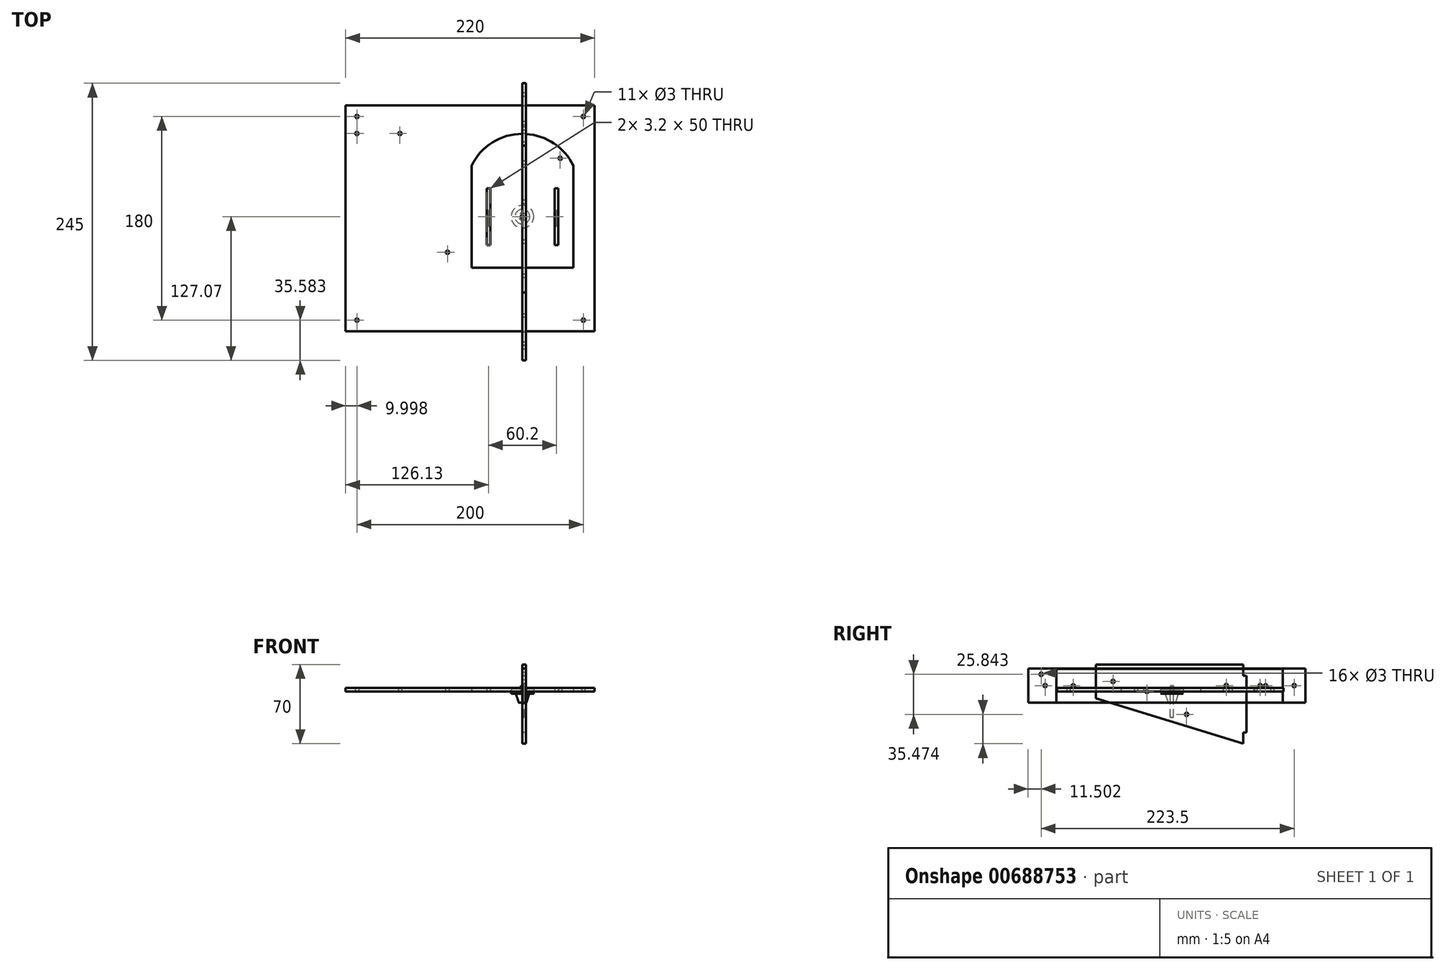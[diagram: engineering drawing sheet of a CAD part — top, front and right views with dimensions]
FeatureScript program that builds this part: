
annotation { "Feature Type Name" : "Feature", "Feature Type Description" : "" }
export const myFeature = defineFeature(function(context is Context, id is Id, definition is map)
    precondition{}
    {
        {
            var Q0;
            Q0=qCreatedBy(makeId("Right.planeOp"),FACE);
            var sketch = newSketch(context, id + "F0", { "sketchPlane" : qUnion([Q0])});
            skLineSegment(sketch, "E0", {"start": v(-67.11, 23.84) * mm, "end": v(62.89, 23.84) * mm});
            skLineSegment(sketch, "E1", {"start": v(-67.11, 23.84) * mm, "end": v(-67.11, -6.16) * mm});
            skLineSegment(sketch, "E2", {"start": v(62.89, 23.84) * mm, "end": v(62.89, -46.16) * mm});
            skLineSegment(sketch, "E3", {"start": v(-67.11, -6.16) * mm, "end": v(62.89, -46.16) * mm});
            skLineSegment(sketch, "E4.bottom", {"start": v(62.89, 13.84) * mm, "end": v(65.89, 13.84) * mm});
            skLineSegment(sketch, "E4.top", {"start": v(62.89, -36.16) * mm, "end": v(65.89, -36.16) * mm});
            skLineSegment(sketch, "E4.left", {"start": v(62.89, 13.84) * mm, "end": v(62.89, -36.16) * mm});
            skLineSegment(sketch, "E4.right", {"start": v(65.89, 13.84) * mm, "end": v(65.89, -36.16) * mm});
            skCircle(sketch, "E5", {"center": v(12.89, -20.32) * mm, "radius": 1.5 * mm});
            skSolve(sketch);
        }
        {
            var Q0;
            Q0=qCreatedBy(makeId("Right.planeOp"),FACE);
            var sketch = newSketch(context, id + "F1", { "sketchPlane" : qUnion([Q0])});
            skLineSegment(sketch, "E6.bottom", {"start": v(-127.07, 20.16) * mm, "end": v(117.93, 20.16) * mm});
            skLineSegment(sketch, "E6.top", {"start": v(-127.07, -9.84) * mm, "end": v(117.93, -9.84) * mm});
            skLineSegment(sketch, "E6.left", {"start": v(-127.07, 20.16) * mm, "end": v(-127.07, -9.84) * mm});
            skLineSegment(sketch, "E6.right", {"start": v(117.93, 20.16) * mm, "end": v(117.93, -9.84) * mm});
            skCircle(sketch, "E7", {"center": v(107.93, 5.16) * mm, "radius": 1.5 * mm});
            skCircle(sketch, "E8", {"center": v(77.93, 5.16) * mm, "radius": 1.5 * mm});
            skCircle(sketch, "E9", {"center": v(-115.57, 15.16) * mm, "radius": 1.5 * mm});
            skSolve(sketch);
        }
        {
            var Q0;
            Q0=qCreatedBy(makeId("Right.planeOp"),FACE);
            var sketch = newSketch(context, id + "F2", { "sketchPlane" : qUnion([Q0])});
            skLineSegment(sketch, "E10.bottom", {"start": v(-102.26, 20) * mm, "end": v(97.74, 20) * mm});
            skLineSegment(sketch, "E10.top", {"start": v(-102.26, -10) * mm, "end": v(97.74, -10) * mm});
            skLineSegment(sketch, "E10.left", {"start": v(-102.26, 20) * mm, "end": v(-102.26, -10) * mm});
            skLineSegment(sketch, "E10.right", {"start": v(97.74, 20) * mm, "end": v(97.74, -10) * mm});
            skCircle(sketch, "E11", {"center": v(-22.26, 0) * mm, "radius": 1.5 * mm});
            skSolve(sketch);
        }
        {
            var Q0;
            Q0=qSketchRegion(id+"F0",true);
            extrude(context, id + "F3", {"entities" : qUnion([Q0]), "depth" : 3.2 * mm});
        }
        {
            var Q0;
            Q0=makeQuery(id+"F1.imprint","IMPRINT",FACE,{"disambiguationData":[TD([[makeQuery(id+"F1.imprint","IMPRINT",EDGE,{"derivedFrom":sQuery(id+"F1.wireOp",EDGE,"E6.bottom")}),-1.0]])]});
            extrude(context, id + "F4", {"entities" : qUnion([Q0]), "depth" : 3.2 * mm});
        }
        {
            var Q0;
            Q0=makeQuery(id+"F2.imprint","IMPRINT",FACE,{"disambiguationData":[TD([[makeQuery(id+"F2.imprint","IMPRINT",EDGE,{"derivedFrom":sQuery(id+"F2.wireOp",EDGE,"E10.bottom")}),-1.0]])]});
            extrude(context, id + "F5", {"entities" : qUnion([Q0]), "depth" : 3.2 * mm});
        }
        {
            var Q0;
            Q0=makeQuery(id+"F3.opExtrude","CAP_FACE",FACE,{"disambiguationData":[OSD([sQuery(id+"F0.wireOp",EDGE,"E0"),sQuery(id+"F0.wireOp",EDGE,"E1"),sQuery(id+"F0.wireOp",EDGE,"E2"),sQuery(id+"F0.wireOp",EDGE,"E3")])],"isStart":false});
            var sketch = newSketch(context, id + "F6", { "sketchPlane" : qUnion([Q0])});
            skCircle(sketch, "E12", {"center": v(-52.11, 8.84) * mm, "radius": 1.5 * mm});
            skSolve(sketch);
        }
        {
            var Q0;
            Q0=makeQuery(id+"F6.imprint","IMPRINT",FACE,{"disambiguationData":[TD([[makeQuery(id+"F6.imprint","IMPRINT",EDGE,{"derivedFrom":sQuery(id+"F6.wireOp",EDGE,"E12")}),1.0]])]});
            extrude(context, id + "F7", {"entities" : qUnion([Q0]), "operationType" : NewBodyOperationType.REMOVE, "endBound" : BoundingType.THROUGH_ALL, "oppositeDirection" : true, "depth" : 25 * mm});
        }
        {
            var Q0;
            Q0=makeQuery(id+"F4.opExtrude","CAP_FACE",FACE,{"disambiguationData":[OSD([sQuery(id+"F1.wireOp",EDGE,"E6.bottom"),sQuery(id+"F1.wireOp",EDGE,"E6.top"),sQuery(id+"F1.wireOp",EDGE,"E6.left"),sQuery(id+"F1.wireOp",EDGE,"E6.right")])],"isStart":false});
            var sketch = newSketch(context, id + "F8", { "sketchPlane" : qUnion([Q0])});
            skCircle(sketch, "E13", {"center": v(-112.07, 5.16) * mm, "radius": 1.5 * mm});
            skCircle(sketch, "E14", {"center": v(47.93, 5.16) * mm, "radius": 1.5 * mm});
            skSolve(sketch);
        }
        {
            var Q0;
            Q0=makeQuery(id+"F8.imprint","IMPRINT",FACE,{"disambiguationData":[TD([[makeQuery(id+"F8.imprint","IMPRINT",EDGE,{"derivedFrom":sQuery(id+"F8.wireOp",EDGE,"E13")}),1.0]])]});
            var Q1;
            Q1=makeQuery(id+"F8.imprint","IMPRINT",FACE,{"disambiguationData":[TD([[makeQuery(id+"F8.imprint","IMPRINT",EDGE,{"derivedFrom":sQuery(id+"F8.wireOp",EDGE,"E14")}),1.0]])]});
            extrude(context, id + "F9", {"entities" : qUnion([Q0, Q1]), "operationType" : NewBodyOperationType.REMOVE, "endBound" : BoundingType.THROUGH_ALL, "oppositeDirection" : true, "depth" : 25 * mm});
        }
        {
            var Q0;
            Q0=makeQuery(id+"F5.opExtrude","CAP_FACE",FACE,{"disambiguationData":[OSD([sQuery(id+"F2.wireOp",EDGE,"E10.bottom"),sQuery(id+"F2.wireOp",EDGE,"E10.top"),sQuery(id+"F2.wireOp",EDGE,"E10.left"),sQuery(id+"F2.wireOp",EDGE,"E10.right")])],"isStart":false});
            var sketch = newSketch(context, id + "F10", { "sketchPlane" : qUnion([Q0])});
            skCircle(sketch, "E15", {"center": v(-87.26, 5) * mm, "radius": 1.5 * mm});
            skCircle(sketch, "E16", {"center": v(82.74, 5) * mm, "radius": 1.5 * mm});
            skSolve(sketch);
        }
        {
            var Q0;
            Q0=makeQuery(id+"F10.imprint","IMPRINT",FACE,{"disambiguationData":[TD([[makeQuery(id+"F10.imprint","IMPRINT",EDGE,{"derivedFrom":sQuery(id+"F10.wireOp",EDGE,"E15")}),1.0]])]});
            var Q1;
            Q1=makeQuery(id+"F10.imprint","IMPRINT",FACE,{"disambiguationData":[TD([[makeQuery(id+"F10.imprint","IMPRINT",EDGE,{"derivedFrom":sQuery(id+"F10.wireOp",EDGE,"E16")}),1.0]])]});
            extrude(context, id + "F11", {"entities" : qUnion([Q0, Q1]), "operationType" : NewBodyOperationType.REMOVE, "endBound" : BoundingType.THROUGH_ALL, "oppositeDirection" : true, "depth" : 25 * mm});
        }
        {
            var Q0;
            Q0=qCreatedBy(makeId("Top.planeOp"),FACE);
            var sketch = newSketch(context, id + "F12", { "sketchPlane" : qUnion([Q0])});
            skLineSegment(sketch, "E17.bottom", {"start": v(-45, 45) * mm, "end": v(45, 45) * mm});
            skLineSegment(sketch, "E17.top", {"start": v(-45, -45) * mm, "end": v(45, -45) * mm});
            skLineSegment(sketch, "E17.left", {"start": v(-45, 45) * mm, "end": v(-45, -45) * mm});
            skLineSegment(sketch, "E17.right", {"start": v(45, 45) * mm, "end": v(45, -45) * mm});
            skLineSegment(sketch, "E18.bottom", {"start": v(-31.7, 25) * mm, "end": v(-28.5, 25) * mm});
            skLineSegment(sketch, "E18.top", {"start": v(-31.7, -25) * mm, "end": v(-28.5, -25) * mm});
            skLineSegment(sketch, "E18.left", {"start": v(-31.7, 25) * mm, "end": v(-31.7, -25) * mm});
            skLineSegment(sketch, "E18.right", {"start": v(-28.5, 25) * mm, "end": v(-28.5, -25) * mm});
            skLineSegment(sketch, "E19.bottom", {"start": v(28.5, 25) * mm, "end": v(31.7, 25) * mm});
            skLineSegment(sketch, "E19.top", {"start": v(28.5, -25) * mm, "end": v(31.7, -25) * mm});
            skLineSegment(sketch, "E19.left", {"start": v(28.5, 25) * mm, "end": v(28.5, -25) * mm});
            skLineSegment(sketch, "E19.right", {"start": v(31.7, 25) * mm, "end": v(31.7, -25) * mm});
            skArc(sketch, "E20", {"start": v(45, 45) * mm, "mid": v(0, 73.2) * mm, "end": v(-45, 45) * mm});
            skCircle(sketch, "E21", {"center": v(33.35, 51.62) * mm, "radius": 1.5 * mm});
            skSolve(sketch);
        }
        {
            var Q0;
            Q0=makeQuery(id+"F12.imprint","IMPRINT",FACE,{"disambiguationData":[TD([[makeQuery(id+"F12.imprint","IMPRINT",EDGE,{"derivedFrom":sQuery(id+"F12.wireOp",EDGE,"E17.bottom")}),-1.0]])]});
            var Q1;
            Q1=makeQuery(id+"F12.imprint","IMPRINT",FACE,{"disambiguationData":[TD([[makeQuery(id+"F12.imprint","IMPRINT",EDGE,{"derivedFrom":sQuery(id+"F12.wireOp",EDGE,"E17.bottom")}),1.0]])]});
            extrude(context, id + "F13", {"entities" : qUnion([Q0, Q1]), "depth" : 3.2 * mm, "offsetDistance" : 25 * mm});
        }
        {
            var Q0;
            Q0=qCreatedBy(makeId("Top.planeOp"),FACE);
            var sketch = newSketch(context, id + "F14", { "sketchPlane" : qUnion([Q0])});
            skLineSegment(sketch, "E22.bottom", {"start": v(-156.23, 98.51) * mm, "end": v(63.77, 98.51) * mm});
            skLineSegment(sketch, "E22.top", {"start": v(-156.23, -101.49) * mm, "end": v(63.77, -101.49) * mm});
            skLineSegment(sketch, "E22.left", {"start": v(-156.23, 98.51) * mm, "end": v(-156.23, -101.49) * mm});
            skLineSegment(sketch, "E22.right", {"start": v(63.77, 98.51) * mm, "end": v(63.77, -101.49) * mm});
            skCircle(sketch, "E23", {"center": v(-146.23, 88.51) * mm, "radius": 1.5 * mm});
            skCircle(sketch, "E24", {"center": v(-146.23, -91.49) * mm, "radius": 1.5 * mm});
            skCircle(sketch, "E25", {"center": v(53.77, 88.51) * mm, "radius": 1.5 * mm});
            skCircle(sketch, "E26", {"center": v(53.77, -91.49) * mm, "radius": 1.5 * mm});
            skCircle(sketch, "E27", {"center": v(-146.23, 73.51) * mm, "radius": 1.5 * mm});
            skCircle(sketch, "E28", {"center": v(-108.23, 73.51) * mm, "radius": 1.5 * mm});
            skSolve(sketch);
        }
        {
            var Q0;
            Q0=qSketchRegion(id+"F14",true);
            extrude(context, id + "F15", {"entities" : qUnion([Q0]), "depth" : 3 * mm, "offsetDistance" : 25 * mm});
        }
        {
            var Q0;
            Q0=makeQuery(id+"F15.opExtrude","CAP_FACE",FACE,{"disambiguationData":[OSD([sQuery(id+"F14.wireOp",EDGE,"E22.bottom"),sQuery(id+"F14.wireOp",EDGE,"E22.top"),sQuery(id+"F14.wireOp",EDGE,"E22.left"),sQuery(id+"F14.wireOp",EDGE,"E22.right")])],"isStart":false});
            var sketch = newSketch(context, id + "F16", { "sketchPlane" : qUnion([Q0])});
            skCircle(sketch, "E29", {"center": v(-66.23, -31.49) * mm, "radius": 1.5 * mm});
            skSolve(sketch);
        }
        {
            var Q0;
            Q0=makeQuery(id+"F16.imprint","IMPRINT",FACE,{"disambiguationData":[TD([[makeQuery(id+"F16.imprint","IMPRINT",EDGE,{"derivedFrom":sQuery(id+"F16.wireOp",EDGE,"E29")}),1.0]])]});
            extrude(context, id + "F17", {"entities" : qUnion([Q0]), "operationType" : NewBodyOperationType.REMOVE, "oppositeDirection" : true, "depth" : 53 * mm, "offsetDistance" : 25 * mm});
        }
        {
            var Q0;
            Q0=makeQuery(id+"F13.opExtrude","CAP_FACE",FACE,{"disambiguationData":[OSD([sQuery(id+"F12.wireOp",EDGE,"E17.bottom"),sQuery(id+"F12.wireOp",EDGE,"E17.top"),sQuery(id+"F12.wireOp",EDGE,"E17.left"),sQuery(id+"F12.wireOp",EDGE,"E17.right")])],"isStart":false});
            var sketch = newSketch(context, id + "F18", { "sketchPlane" : qUnion([Q0])});
            skCircle(sketch, "E30", {"center": v(0, 0) * mm, "radius": 1.5 * mm});
            skSolve(sketch);
        }
        {
            var Q0;
            Q0=makeQuery(id+"F18.imprint","IMPRINT",FACE,{"disambiguationData":[TD([[makeQuery(id+"F18.imprint","IMPRINT",EDGE,{"derivedFrom":sQuery(id+"F18.wireOp",EDGE,"E30")}),1.0]])]});
            extrude(context, id + "F19", {"entities" : qUnion([Q0]), "operationType" : NewBodyOperationType.REMOVE, "oppositeDirection" : true, "depth" : 25 * mm, "offsetDistance" : 25 * mm});
        }
        {
            var Q0;
            Q0=qCreatedBy(makeId("Top.planeOp"),FACE);
            var sketch = newSketch(context, id + "F20", { "sketchPlane" : qUnion([Q0])});
            skCircle(sketch, "E31", {"center": v(0, 0) * mm, "radius": 10 * mm});
            skSolve(sketch);
        }
        {
            var Q0;
            Q0=makeQuery(id+"F20.imprint","IMPRINT",FACE,{"disambiguationData":[TD([[makeQuery(id+"F20.imprint","IMPRINT",EDGE,{"derivedFrom":sQuery(id+"F20.wireOp",EDGE,"E31")}),1.0]])]});
            extrude(context, id + "F21", {"entities" : qUnion([Q0]), "depth" : 4 * mm, "offsetDistance" : 25 * mm, "symmetric" : true});
        }
        {
            var Q0;
            Q0=makeQuery(id+"F21.opExtrude","CAP_FACE",FACE,{"disambiguationData":[OSD([sQuery(id+"F20.wireOp",EDGE,"E31")])],"isStart":false});
            var sketch = newSketch(context, id + "F22", { "sketchPlane" : qUnion([Q0])});
            skCircle(sketch, "E32", {"center": v(0, 0) * mm, "radius": 1.5 * mm});
            skSolve(sketch);
        }
        {
            var Q0;
            Q0=makeQuery(id+"F22.imprint","IMPRINT",FACE,{"disambiguationData":[TD([[makeQuery(id+"F22.imprint","IMPRINT",EDGE,{"derivedFrom":sQuery(id+"F22.wireOp",EDGE,"E32")}),1.0]])]});
            extrude(context, id + "F23", {"entities" : qUnion([Q0]), "operationType" : NewBodyOperationType.REMOVE, "oppositeDirection" : true, "depth" : 25 * mm, "offsetDistance" : 25 * mm});
        }
        {
            var Q0;
            Q0=qCreatedBy(makeId("Front.planeOp"),FACE);
            var sketch = newSketch(context, id + "F24", { "sketchPlane" : qUnion([Q0])});
            skLineSegment(sketch, "E33", {"start": v(0, -15.89) * mm, "end": v(0, 25.02) * mm, "construction": true});
            skLineSegment(sketch, "E34", {"start": v(-6.5, 0) * mm, "end": v(0, 0) * mm});
            skLineSegment(sketch, "E35", {"start": v(0, 0) * mm, "end": v(0, -10) * mm});
            skLineSegment(sketch, "E36", {"start": v(0, -10) * mm, "end": v(-3.23, -10) * mm});
            skLineSegment(sketch, "E37", {"start": v(-3.23, -10) * mm, "end": v(-6.5, 0) * mm});
            skLineSegment(sketch, "E38", {"start": v(-1.5, 0) * mm, "end": v(-1.5, 5) * mm});
            skLineSegment(sketch, "E39", {"start": v(-1.5, 5) * mm, "end": v(0, 5) * mm});
            skLineSegment(sketch, "E40", {"start": v(0, 5) * mm, "end": v(0, 0) * mm});
            skSolve(sketch);
        }
        {
            var Q0;
            Q0=qSketchRegion(id+"F24",true);
            var Q1;
            Q1=sQuery(id+"F24.wireOp",EDGE,"E33");
            revolve(context, id + "F25", {"entities" : qUnion([Q0]), "axis" : qUnion([Q1]), "revolveType" : RevolveType.FULL});
        }
    });
